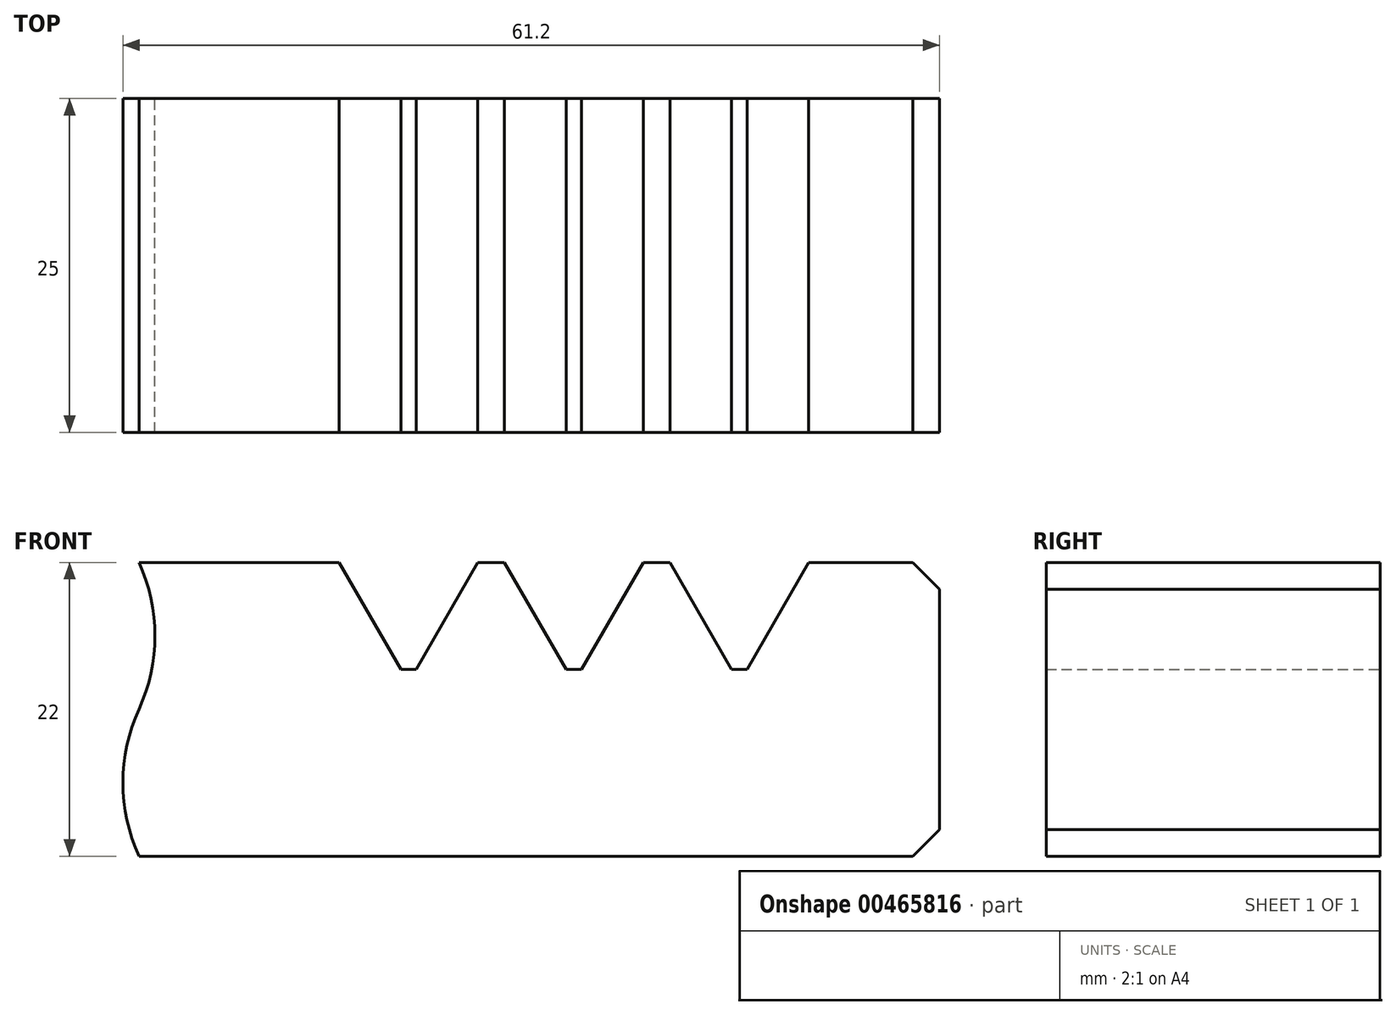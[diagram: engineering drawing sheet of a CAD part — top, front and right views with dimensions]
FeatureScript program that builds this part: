
annotation { "Feature Type Name" : "Feature", "Feature Type Description" : "" }
export const myFeature = defineFeature(function(context is Context, id is Id, definition is map)
    precondition{}
    {
        {
            var Q0;
            Q0=qCreatedBy(makeId("Front.planeOp"),FACE);
            var sketch = newSketch(context, id + "F0", { "sketchPlane" : qUnion([Q0])});
            skLineSegment(sketch, "E0", {"start": v(92.78, 33.21) * mm, "end": v(107.78, 33.21) * mm});
            skLineSegment(sketch, "E1", {"start": v(107.78, 33.21) * mm, "end": v(112.98, 24.21) * mm});
            skLineSegment(sketch, "E2", {"start": v(112.98, 24.21) * mm, "end": v(118.18, 33.21) * mm});
            skLineSegment(sketch, "E3", {"start": v(118.18, 33.21) * mm, "end": v(120.18, 33.21) * mm});
            skLineSegment(sketch, "E4", {"start": v(150.78, 33.21) * mm, "end": v(152.78, 31.21) * mm});
            skArc(sketch, "E5", {"start": v(92.78, 22.21) * mm, "mid": v(93.98, 27.71) * mm, "end": v(92.78, 33.21) * mm});
            skLineSegment(sketch, "E6", {"start": v(80.78, 27.71) * mm, "end": v(104.78, 16.71) * mm, "construction": true});
            skArc(sketch, "E7", {"start": v(92.78, 22.21) * mm, "mid": v(91.58, 16.71) * mm, "end": v(92.78, 11.21) * mm});
            skLineSegment(sketch, "E8", {"start": v(74.79, 33.21) * mm, "end": v(74.79, 11.21) * mm, "construction": true});
            skPoint(sketch, "E9", {"position": v(74.79, 22.21) * mm});
            skPoint(sketch, "E10", {"position": v(92.78, 22.21) * mm});
            skLineSegment(sketch, "E11", {"start": v(107.78, 53.7) * mm, "end": v(118.18, 53.7) * mm, "construction": true});
            skPoint(sketch, "E12", {"position": v(112.98, 53.7) * mm});
            skLineSegment(sketch, "E13", {"start": v(152.78, 31.21) * mm, "end": v(152.78, 22.21) * mm});
            skLineSegment(sketch, "E14", {"start": v(69.18, 22.21) * mm, "end": v(55.9, 22.21) * mm, "construction": true});
            skLineSegment(sketch, "E15.MirrorCS", {"start": v(152.78, 13.21) * mm, "end": v(152.78, 22.21) * mm});
            skLineSegment(sketch, "E16.MirrorCS", {"start": v(150.78, 11.21) * mm, "end": v(152.78, 13.21) * mm});
            skLineSegment(sketch, "E17", {"start": v(119.18, 33.21) * mm, "end": v(119.18, 49.4) * mm});
            skLineSegment(sketch, "E18.MirrorCS", {"start": v(130.57, 33.21) * mm, "end": v(125.95, 25.21) * mm});
            skLineSegment(sketch, "E19.MirrorCS", {"start": v(124.8, 25.21) * mm, "end": v(120.18, 33.21) * mm});
            skLineSegment(sketch, "E20", {"start": v(112.4, 25.21) * mm, "end": v(113.56, 25.21) * mm});
            skLineSegment(sketch, "E21.MirrorCS", {"start": v(125.95, 25.21) * mm, "end": v(124.8, 25.21) * mm});
            skLineSegment(sketch, "E22", {"start": v(92.78, 11.21) * mm, "end": v(150.78, 11.21) * mm});
            skLineSegment(sketch, "E23.trimOffspring", {"start": v(130.57, 33.21) * mm, "end": v(132.57, 33.21) * mm});
            skPoint(sketch, "E24.orphan", {"position": v(125.37, 24.21) * mm});
            skLineSegment(sketch, "E25", {"start": v(131.57, 33.21) * mm, "end": v(131.57, 42.5) * mm});
            skLineSegment(sketch, "E26.MirrorCS", {"start": v(132.57, 33.21) * mm, "end": v(137.19, 25.21) * mm});
            skLineSegment(sketch, "E27.MirrorCS", {"start": v(137.19, 25.21) * mm, "end": v(138.34, 25.21) * mm});
            skLineSegment(sketch, "E28.MirrorCS", {"start": v(138.34, 25.21) * mm, "end": v(142.96, 33.21) * mm});
            skLineSegment(sketch, "E29.trimOffspring", {"start": v(142.96, 33.21) * mm, "end": v(150.78, 33.21) * mm});
            skSolve(sketch);
        }
        {
            var Q0;
            Q0=makeQuery(id+"F0.imprint","IMPRINT",FACE,{"disambiguationData":[TD([[makeQuery(id+"F0.imprint","IMPRINT",EDGE,{"derivedFrom":sQuery(id+"F0.wireOp",EDGE,"E0")}),-1.0]])]});
            var Q1;
            {var subQ3=sQuery(id+"F0.wireOp",EDGE,"E20");Q1=makeQuery(id+"F0.imprint","IMPRINT",FACE,{"disambiguationData":[TD([[makeQuery(id+"F0.imprint","IMPRINT",EDGE,{"derivedFrom":subQ3}),-1.0]])]});}
            var Q2;
            {var subQ3=sQuery(id+"F0.wireOp",EDGE,"E21.MirrorCS");Q2=makeQuery(id+"F0.imprint","IMPRINT",FACE,{"disambiguationData":[TD([[makeQuery(id+"F0.imprint","IMPRINT",EDGE,{"derivedFrom":subQ3}),1.0]])]});}
            extrude(context, id + "F1", {"entities" : qUnion([Q0, Q1, Q2]), "depth" : 25 * mm});
        }
    });
